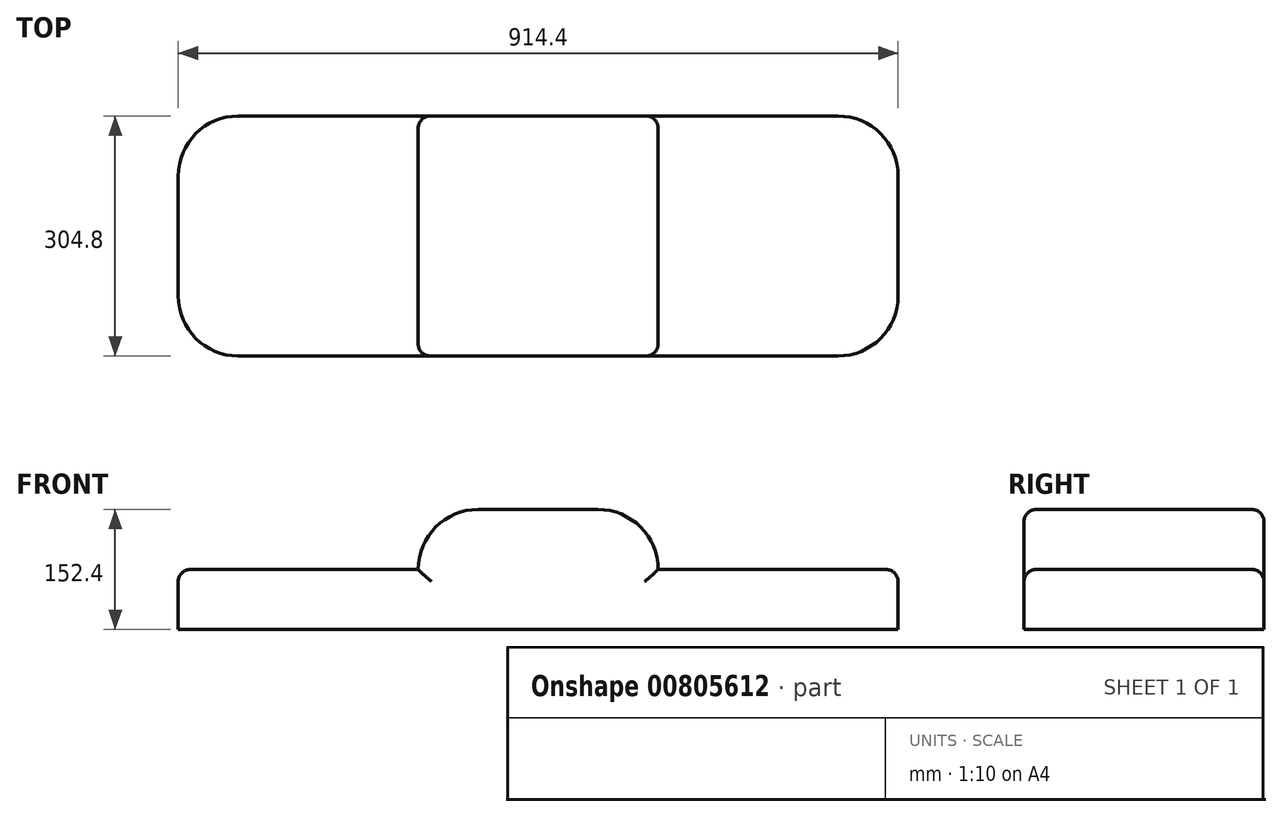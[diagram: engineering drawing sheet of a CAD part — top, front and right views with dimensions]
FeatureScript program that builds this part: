
annotation { "Feature Type Name" : "Feature", "Feature Type Description" : "" }
export const myFeature = defineFeature(function(context is Context, id is Id, definition is map)
    precondition{}
    {
        {
            var Q0;
            Q0=qCreatedBy(makeId("Top.planeOp"),FACE);
            var sketch = newSketch(context, id + "F0", { "sketchPlane" : qUnion([Q0])});
            skLineSegment(sketch, "E0", {"start": v(-63.6, 36.64) * mm, "end": v(850.8, 36.64) * mm});
            skLineSegment(sketch, "E1", {"start": v(850.8, 36.64) * mm, "end": v(850.8, -268.16) * mm});
            skLineSegment(sketch, "E2", {"start": v(850.8, -268.16) * mm, "end": v(-63.6, -268.16) * mm});
            skLineSegment(sketch, "E3", {"start": v(-63.6, -268.16) * mm, "end": v(-63.6, 36.64) * mm});
            skSolve(sketch);
        }
        {
            var Q0;
            Q0 = qSketchRegion(id + "F0", true);
            extrude(context, id + "F1", {"entities" : qUnion([Q0]), "depth" : 76.2 * mm, "offsetDistance" : 30.48 * mm});
        }
        {
            var Q0;
            Q0=makeQuery(id+"F1.opExtrude","CAP_FACE",FACE,{"disambiguationData":[OSD([sQuery(id+"F0.wireOp",EDGE,"E0"),sQuery(id+"F0.wireOp",EDGE,"E1"),sQuery(id+"F0.wireOp",EDGE,"E2"),sQuery(id+"F0.wireOp",EDGE,"E3")])],"isStart":false});
            var sketch = newSketch(context, id + "F2", { "sketchPlane" : qUnion([Q0])});
            skLineSegment(sketch, "E4", {"start": v(241.2, 36.64) * mm, "end": v(241.2, -268.16) * mm});
            skLineSegment(sketch, "E5", {"start": v(241.2, -268.16) * mm, "end": v(546, -268.16) * mm});
            skLineSegment(sketch, "E6", {"start": v(546, -268.16) * mm, "end": v(546, 36.64) * mm});
            skLineSegment(sketch, "E7", {"start": v(546, 36.64) * mm, "end": v(241.2, 36.64) * mm});
            skSolve(sketch);
        }
        {
            var Q0;
            Q0=makeQuery(id+"F2.imprint","IMPRINT",FACE,{"disambiguationData":[TD([[makeQuery(id+"F2.imprint","IMPRINT",EDGE,{"derivedFrom":sQuery(id+"F2.wireOp",EDGE,"E4")}),1.0]])]});
            extrude(context, id + "F3", {"entities" : qUnion([Q0]), "operationType" : NewBodyOperationType.ADD, "depth" : 76.2 * mm, "offsetDistance" : 30.48 * mm});
        }
        {
            var Q0;
            Q0=makeQuery(id+"F3.opExtrude","CAP_EDGE",EDGE,{"disambiguationData":[OSD([sQuery(id+"F2.wireOp",EDGE,"E6")])],"isStart":false});
            var Q1;
            Q1=makeQuery(id+"F3.opExtrude","CAP_EDGE",EDGE,{"disambiguationData":[OSD([sQuery(id+"F2.wireOp",EDGE,"E4")])],"isStart":false});
            fillet(context, id + "F4", {"entities" : qUnion([Q0, Q1]), "radius" : 76.2 * mm, "tangentPropagation" : true, "allowEdgeOverflow" : false});
        }
        {
            var Q0;
            Q0=makeQuery(id+"F1.opExtrude","SWEPT_EDGE",EDGE,{"disambiguationData":[OSD([sQuery(id+"F0.wireOp",EDGE,"E0"),sQuery(id+"F0.wireOp",EDGE,"E1")])]});
            var Q1;
            Q1=makeQuery(id+"F1.opExtrude","SWEPT_EDGE",EDGE,{"disambiguationData":[OSD([sQuery(id+"F0.wireOp",EDGE,"E1"),sQuery(id+"F0.wireOp",EDGE,"E2")])]});
            var Q2;
            Q2=makeQuery(id+"F1.opExtrude","SWEPT_EDGE",EDGE,{"disambiguationData":[OSD([sQuery(id+"F0.wireOp",EDGE,"E0"),sQuery(id+"F0.wireOp",EDGE,"E3")])]});
            var Q3;
            Q3=makeQuery(id+"F1.opExtrude","SWEPT_EDGE",EDGE,{"disambiguationData":[OSD([sQuery(id+"F0.wireOp",EDGE,"E2"),sQuery(id+"F0.wireOp",EDGE,"E3")])]});
            fillet(context, id + "F5", {"entities" : qUnion([Q0, Q1, Q2, Q3]), "radius" : 76.2 * mm, "tangentPropagation" : true, "allowEdgeOverflow" : false});
        }
        {
            var Q0;
            Q0=makeQuery(id+"F1.opExtrude","CAP_EDGE",EDGE,{"disambiguationData":[OSD([sQuery(id+"F0.wireOp",EDGE,"E1")])],"isStart":false});
            var Q1;
            {var subQ0=sQuery(id+"F0.wireOp",EDGE,"E2");var subQ1=sQuery(id+"F0.wireOp",EDGE,"E1");var subQ2=sQuery(id+"F0.wireOp",EDGE,"E0");Q1=makeQuery(id+"F5.opFillet","BLEND_EDGE",EDGE,{"blendedFrom":[makeQuery(id+"F1.opExtrude","SWEPT_EDGE",EDGE,{"disambiguationData":[OSD([subQ1,subQ0])]}),makeQuery(id+"F3.boolean.opBoolean","SPLIT",FACE,{"disambiguationData":[TD([makeQuery(id+"F1.opExtrude","SWEPT_FACE",FACE,{"disambiguationData":[OSD([subQ1])]})])],"derivedFrom":makeQuery(id+"F1.opExtrude","CAP_FACE",FACE,{"disambiguationData":[OSD([subQ2,subQ1,subQ0,sQuery(id+"F0.wireOp",EDGE,"E3")])],"isStart":false})})],"blendedInto":[makeQuery(id+"F3.boolean.opBoolean","SPLIT",FACE,{"disambiguationData":[TD([makeQuery(id+"F1.opExtrude","SWEPT_FACE",FACE,{"disambiguationData":[OSD([subQ1])]})])],"derivedFrom":makeQuery(id+"F1.opExtrude","CAP_FACE",FACE,{"disambiguationData":[OSD([subQ2,subQ1,subQ0,sQuery(id+"F0.wireOp",EDGE,"E3")])],"isStart":false})})]});}
            var Q2;
            {var subQ0=sQuery(id+"F0.wireOp",EDGE,"E2");var subQ1=sQuery(id+"F0.wireOp",EDGE,"E1");Q2=makeQuery(id+"F3.boolean.opBoolean","SPLIT",EDGE,{"disambiguationData":[TD([makeQuery(id+"F1.opExtrude","SWEPT_FACE",FACE,{"disambiguationData":[OSD([subQ1])]})])],"derivedFrom":makeQuery(id+"F1.opExtrude","CAP_EDGE",EDGE,{"disambiguationData":[OSD([subQ0])],"isStart":false})});}
            var Q3;
            {var subQ0=sQuery(id+"F0.wireOp",EDGE,"E2");var subQ1=sQuery(id+"F0.wireOp",EDGE,"E1");var subQ2=sQuery(id+"F0.wireOp",EDGE,"E0");Q3=makeQuery(id+"F5.opFillet","BLEND_EDGE",EDGE,{"blendedFrom":[makeQuery(id+"F1.opExtrude","SWEPT_EDGE",EDGE,{"disambiguationData":[OSD([subQ2,subQ1])]}),makeQuery(id+"F3.boolean.opBoolean","SPLIT",FACE,{"disambiguationData":[TD([makeQuery(id+"F1.opExtrude","SWEPT_FACE",FACE,{"disambiguationData":[OSD([subQ1])]})])],"derivedFrom":makeQuery(id+"F1.opExtrude","CAP_FACE",FACE,{"disambiguationData":[OSD([subQ2,subQ1,subQ0,sQuery(id+"F0.wireOp",EDGE,"E3")])],"isStart":false})})],"blendedInto":[makeQuery(id+"F3.boolean.opBoolean","SPLIT",FACE,{"disambiguationData":[TD([makeQuery(id+"F1.opExtrude","SWEPT_FACE",FACE,{"disambiguationData":[OSD([subQ1])]})])],"derivedFrom":makeQuery(id+"F1.opExtrude","CAP_FACE",FACE,{"disambiguationData":[OSD([subQ2,subQ1,subQ0,sQuery(id+"F0.wireOp",EDGE,"E3")])],"isStart":false})})]});}
            var Q4;
            {var subQ0=sQuery(id+"F0.wireOp",EDGE,"E1");var subQ1=sQuery(id+"F0.wireOp",EDGE,"E0");Q4=makeQuery(id+"F3.boolean.opBoolean","SPLIT",EDGE,{"disambiguationData":[TD([makeQuery(id+"F1.opExtrude","SWEPT_FACE",FACE,{"disambiguationData":[OSD([subQ0])]})])],"derivedFrom":makeQuery(id+"F1.opExtrude","CAP_EDGE",EDGE,{"disambiguationData":[OSD([subQ1])],"isStart":false})});}
            var Q5;
            Q5=makeQuery(id+"F4.opFillet","BLEND_EDGE",EDGE,{"blendedFrom":[makeQuery(id+"F3.opExtrude","CAP_EDGE",EDGE,{"disambiguationData":[OSD([sQuery(id+"F2.wireOp",EDGE,"E6")])],"isStart":false}),makeQuery(id+"F3.boolean.opBoolean","MERGE",FACE,{"derivedFrom":[makeQuery(id+"F1.opExtrude","SWEPT_FACE",FACE,{"disambiguationData":[OSD([sQuery(id+"F0.wireOp",EDGE,"E0")])]}),makeQuery(id+"F3.opExtrude","SWEPT_FACE",FACE,{"disambiguationData":[OSD([sQuery(id+"F2.wireOp",EDGE,"E7")])]})]})],"blendedInto":[makeQuery(id+"F3.boolean.opBoolean","MERGE",FACE,{"derivedFrom":[makeQuery(id+"F1.opExtrude","SWEPT_FACE",FACE,{"disambiguationData":[OSD([sQuery(id+"F0.wireOp",EDGE,"E0")])]}),makeQuery(id+"F3.opExtrude","SWEPT_FACE",FACE,{"disambiguationData":[OSD([sQuery(id+"F2.wireOp",EDGE,"E7")])]})]})]});
            var Q6;
            Q6=makeQuery(id+"F4.opFillet","BLEND_EDGE",EDGE,{"blendedFrom":[makeQuery(id+"F3.opExtrude","CAP_EDGE",EDGE,{"disambiguationData":[OSD([sQuery(id+"F2.wireOp",EDGE,"E6")])],"isStart":false}),makeQuery(id+"F3.boolean.opBoolean","MERGE",FACE,{"derivedFrom":[makeQuery(id+"F1.opExtrude","SWEPT_FACE",FACE,{"disambiguationData":[OSD([sQuery(id+"F0.wireOp",EDGE,"E2")])]}),makeQuery(id+"F3.opExtrude","SWEPT_FACE",FACE,{"disambiguationData":[OSD([sQuery(id+"F2.wireOp",EDGE,"E5")])]})]})],"blendedInto":[makeQuery(id+"F3.boolean.opBoolean","MERGE",FACE,{"derivedFrom":[makeQuery(id+"F1.opExtrude","SWEPT_FACE",FACE,{"disambiguationData":[OSD([sQuery(id+"F0.wireOp",EDGE,"E2")])]}),makeQuery(id+"F3.opExtrude","SWEPT_FACE",FACE,{"disambiguationData":[OSD([sQuery(id+"F2.wireOp",EDGE,"E5")])]})]})]});
            var Q7;
            Q7=makeQuery(id+"F3.opExtrude","CAP_EDGE",EDGE,{"disambiguationData":[OSD([sQuery(id+"F2.wireOp",EDGE,"E5")])],"isStart":false});
            var Q8;
            Q8=makeQuery(id+"F3.opExtrude","CAP_EDGE",EDGE,{"disambiguationData":[OSD([sQuery(id+"F2.wireOp",EDGE,"E7")])],"isStart":false});
            var Q9;
            Q9=makeQuery(id+"F4.opFillet","BLEND_EDGE",EDGE,{"blendedFrom":[makeQuery(id+"F3.opExtrude","CAP_EDGE",EDGE,{"disambiguationData":[OSD([sQuery(id+"F2.wireOp",EDGE,"E4")])],"isStart":false}),makeQuery(id+"F3.boolean.opBoolean","MERGE",FACE,{"derivedFrom":[makeQuery(id+"F1.opExtrude","SWEPT_FACE",FACE,{"disambiguationData":[OSD([sQuery(id+"F0.wireOp",EDGE,"E0")])]}),makeQuery(id+"F3.opExtrude","SWEPT_FACE",FACE,{"disambiguationData":[OSD([sQuery(id+"F2.wireOp",EDGE,"E7")])]})]})],"blendedInto":[makeQuery(id+"F3.boolean.opBoolean","MERGE",FACE,{"derivedFrom":[makeQuery(id+"F1.opExtrude","SWEPT_FACE",FACE,{"disambiguationData":[OSD([sQuery(id+"F0.wireOp",EDGE,"E0")])]}),makeQuery(id+"F3.opExtrude","SWEPT_FACE",FACE,{"disambiguationData":[OSD([sQuery(id+"F2.wireOp",EDGE,"E7")])]})]})]});
            var Q10;
            Q10=makeQuery(id+"F4.opFillet","BLEND_EDGE",EDGE,{"blendedFrom":[makeQuery(id+"F3.opExtrude","CAP_EDGE",EDGE,{"disambiguationData":[OSD([sQuery(id+"F2.wireOp",EDGE,"E4")])],"isStart":false}),makeQuery(id+"F3.boolean.opBoolean","MERGE",FACE,{"derivedFrom":[makeQuery(id+"F1.opExtrude","SWEPT_FACE",FACE,{"disambiguationData":[OSD([sQuery(id+"F0.wireOp",EDGE,"E2")])]}),makeQuery(id+"F3.opExtrude","SWEPT_FACE",FACE,{"disambiguationData":[OSD([sQuery(id+"F2.wireOp",EDGE,"E5")])]})]})],"blendedInto":[makeQuery(id+"F3.boolean.opBoolean","MERGE",FACE,{"derivedFrom":[makeQuery(id+"F1.opExtrude","SWEPT_FACE",FACE,{"disambiguationData":[OSD([sQuery(id+"F0.wireOp",EDGE,"E2")])]}),makeQuery(id+"F3.opExtrude","SWEPT_FACE",FACE,{"disambiguationData":[OSD([sQuery(id+"F2.wireOp",EDGE,"E5")])]})]})]});
            var Q11;
            {var subQ0=sQuery(id+"F0.wireOp",EDGE,"E3");var subQ1=sQuery(id+"F0.wireOp",EDGE,"E0");Q11=makeQuery(id+"F3.boolean.opBoolean","SPLIT",EDGE,{"disambiguationData":[TD([makeQuery(id+"F1.opExtrude","SWEPT_FACE",FACE,{"disambiguationData":[OSD([subQ0])]})])],"derivedFrom":makeQuery(id+"F1.opExtrude","CAP_EDGE",EDGE,{"disambiguationData":[OSD([subQ1])],"isStart":false})});}
            var Q12;
            {var subQ0=sQuery(id+"F0.wireOp",EDGE,"E2");var subQ1=sQuery(id+"F0.wireOp",EDGE,"E3");var subQ2=sQuery(id+"F0.wireOp",EDGE,"E0");Q12=makeQuery(id+"F5.opFillet","BLEND_EDGE",EDGE,{"blendedFrom":[makeQuery(id+"F1.opExtrude","SWEPT_EDGE",EDGE,{"disambiguationData":[OSD([subQ2,subQ1])]}),makeQuery(id+"F3.boolean.opBoolean","SPLIT",FACE,{"disambiguationData":[TD([makeQuery(id+"F1.opExtrude","SWEPT_FACE",FACE,{"disambiguationData":[OSD([subQ1])]})])],"derivedFrom":makeQuery(id+"F1.opExtrude","CAP_FACE",FACE,{"disambiguationData":[OSD([subQ2,sQuery(id+"F0.wireOp",EDGE,"E1"),subQ0,subQ1])],"isStart":false})})],"blendedInto":[makeQuery(id+"F3.boolean.opBoolean","SPLIT",FACE,{"disambiguationData":[TD([makeQuery(id+"F1.opExtrude","SWEPT_FACE",FACE,{"disambiguationData":[OSD([subQ1])]})])],"derivedFrom":makeQuery(id+"F1.opExtrude","CAP_FACE",FACE,{"disambiguationData":[OSD([subQ2,sQuery(id+"F0.wireOp",EDGE,"E1"),subQ0,subQ1])],"isStart":false})})]});}
            var Q13;
            Q13=makeQuery(id+"F1.opExtrude","CAP_EDGE",EDGE,{"disambiguationData":[OSD([sQuery(id+"F0.wireOp",EDGE,"E3")])],"isStart":false});
            var Q14;
            {var subQ0=sQuery(id+"F0.wireOp",EDGE,"E2");var subQ1=sQuery(id+"F0.wireOp",EDGE,"E3");var subQ2=sQuery(id+"F0.wireOp",EDGE,"E0");Q14=makeQuery(id+"F5.opFillet","BLEND_EDGE",EDGE,{"blendedFrom":[makeQuery(id+"F1.opExtrude","SWEPT_EDGE",EDGE,{"disambiguationData":[OSD([subQ0,subQ1])]}),makeQuery(id+"F3.boolean.opBoolean","SPLIT",FACE,{"disambiguationData":[TD([makeQuery(id+"F1.opExtrude","SWEPT_FACE",FACE,{"disambiguationData":[OSD([subQ1])]})])],"derivedFrom":makeQuery(id+"F1.opExtrude","CAP_FACE",FACE,{"disambiguationData":[OSD([subQ2,sQuery(id+"F0.wireOp",EDGE,"E1"),subQ0,subQ1])],"isStart":false})})],"blendedInto":[makeQuery(id+"F3.boolean.opBoolean","SPLIT",FACE,{"disambiguationData":[TD([makeQuery(id+"F1.opExtrude","SWEPT_FACE",FACE,{"disambiguationData":[OSD([subQ1])]})])],"derivedFrom":makeQuery(id+"F1.opExtrude","CAP_FACE",FACE,{"disambiguationData":[OSD([subQ2,sQuery(id+"F0.wireOp",EDGE,"E1"),subQ0,subQ1])],"isStart":false})})]});}
            var Q15;
            {var subQ0=sQuery(id+"F0.wireOp",EDGE,"E3");var subQ1=sQuery(id+"F0.wireOp",EDGE,"E2");Q15=makeQuery(id+"F3.boolean.opBoolean","SPLIT",EDGE,{"disambiguationData":[TD([makeQuery(id+"F1.opExtrude","SWEPT_FACE",FACE,{"disambiguationData":[OSD([subQ0])]})])],"derivedFrom":makeQuery(id+"F1.opExtrude","CAP_EDGE",EDGE,{"disambiguationData":[OSD([subQ1])],"isStart":false})});}
            fillet(context, id + "F6", {"entities" : qUnion([Q0, Q1, Q2, Q3, Q4, Q5, Q6, Q7, Q8, Q9, Q10, Q11, Q12, Q13, Q14, Q15]), "radius" : 15.24 * mm, "tangentPropagation" : true, "allowEdgeOverflow" : false});
        }
    });
